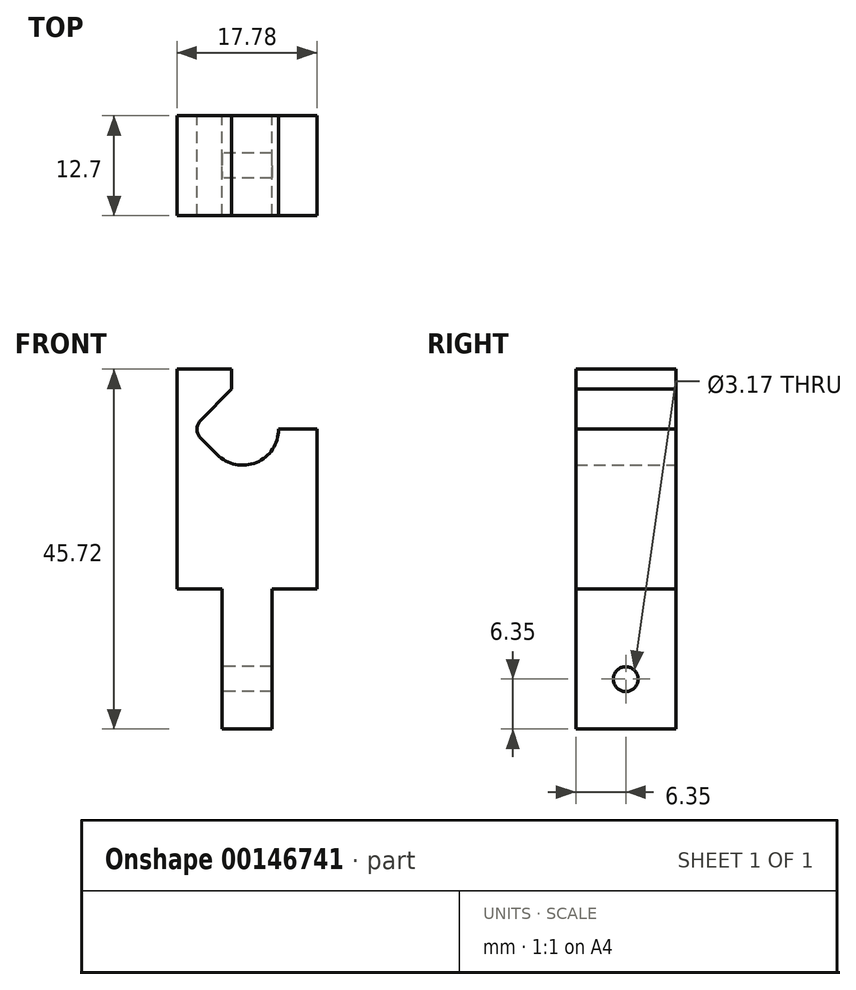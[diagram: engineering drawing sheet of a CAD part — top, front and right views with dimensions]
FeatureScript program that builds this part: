
annotation { "Feature Type Name" : "Feature", "Feature Type Description" : "" }
export const myFeature = defineFeature(function(context is Context, id is Id, definition is map)
    precondition{}
    {
        {
            var Q0;
            Q0=qCreatedBy(makeId("Front.planeOp"),FACE);
            var sketch = newSketch(context, id + "F0", { "sketchPlane" : qUnion([Q0])});
            skLineSegment(sketch, "E0.top", {"start": v(3.17, -17.78) * mm, "end": v(-3.17, -17.78) * mm});
            skLineSegment(sketch, "E0.left", {"start": v(8.9, 20.32) * mm, "end": v(8.9, 0) * mm});
            skLineSegment(sketch, "E0.right", {"start": v(-8.9, 27.94) * mm, "end": v(-8.89, 0) * mm});
            skLineSegment(sketch, "E1", {"start": v(-8.9, 0) * mm, "end": v(-3.17, 0) * mm});
            skLineSegment(sketch, "E2", {"start": v(3.17, 0) * mm, "end": v(8.9, 0) * mm});
            skLineSegment(sketch, "E3", {"start": v(8.9, 20.32) * mm, "end": v(-8.9, 20.32) * mm, "construction": true});
            skArc(sketch, "E4", {"start": v(-5.89, 21.44) * mm, "mid": v(-6.35, 20.32) * mm, "end": v(-5.89, 19.2) * mm});
            skLineSegment(sketch, "E5", {"start": v(-3.77, 17.09) * mm, "end": v(-5.89, 19.2) * mm});
            skArc(sketch, "E6", {"start": v(-3.77, 17.09) * mm, "mid": v(1.2, 16.1) * mm, "end": v(4.03, 20.32) * mm});
            skLineSegment(sketch, "E7", {"start": v(3.17, 0) * mm, "end": v(3.18, -17.78) * mm});
            skPoint(sketch, "E8.start.orphan", {"position": v(0, 0) * mm});
            skLineSegment(sketch, "E9", {"start": v(-3.17, 0) * mm, "end": v(-3.17, -17.78) * mm});
            skLineSegment(sketch, "E10", {"start": v(0, 0) * mm, "end": v(0, -17.78) * mm, "construction": true});
            skLineSegment(sketch, "E11", {"start": v(-1.93, 27.94) * mm, "end": v(-1.93, 25.4) * mm});
            skLineSegment(sketch, "E12", {"start": v(-1.93, 25.4) * mm, "end": v(-5.89, 21.44) * mm});
            skLineSegment(sketch, "E13.trimOffspring", {"start": v(-1.93, 27.94) * mm, "end": v(-8.9, 27.94) * mm});
            skCircle(sketch, "E14", {"center": v(-4.76, 20.32) * mm, "radius": 1.59 * mm, "construction": true});
            skCircle(sketch, "E15", {"center": v(-1.44, 20.32) * mm, "radius": 3.94 * mm, "construction": true});
            skLineSegment(sketch, "E16", {"start": v(8.9, 20.32) * mm, "end": v(4.03, 20.32) * mm});
            skSolve(sketch);
        }
        {
            var Q0;
            Q0 = qSketchRegion(id + "F0", true);
            extrude(context, id + "F1", {"entities" : qUnion([Q0]), "endBound" : BoundingType.SYMMETRIC, "depth" : 12.7 * mm});
        }
        {
            var Q0;
            Q0=makeQuery(id+"F1.opExtrude","SWEPT_FACE",FACE,{"disambiguationData":[OSD([sQuery(id+"F0.wireOp",EDGE,"E9")])]});
            var sketch = newSketch(context, id + "F2", { "sketchPlane" : qUnion([Q0])});
            skLineSegment(sketch, "E17", {"start": v(3, -11.43) * mm, "end": v(-3, -11.43) * mm, "construction": true});
            skLineSegment(sketch, "E18", {"start": v(0, -17.78) * mm, "end": v(0, -11.43) * mm, "construction": true});
            skCircle(sketch, "E19", {"center": v(0, -11.43) * mm, "radius": 1.59 * mm});
            skSolve(sketch);
        }
        {
            var Q0;
            Q0 = qSketchRegion(id + "F2", true);
            extrude(context, id + "F3", {"entities" : qUnion([Q0]), "operationType" : NewBodyOperationType.REMOVE, "endBound" : BoundingType.THROUGH_ALL, "oppositeDirection" : true, "depth" : 25.4 * mm});
        }
        {
            var Q0;
            Q0=qCreatedBy(makeId("Top.planeOp"),FACE);
            var sketch = newSketch(context, id + "F4", { "sketchPlane" : qUnion([Q0])});
            skLineSegment(sketch, "E20", {"start": v(-58.84, 18.1) * mm, "end": v(54.16, 50.27) * mm});
            skSolve(sketch);
        }
    });
